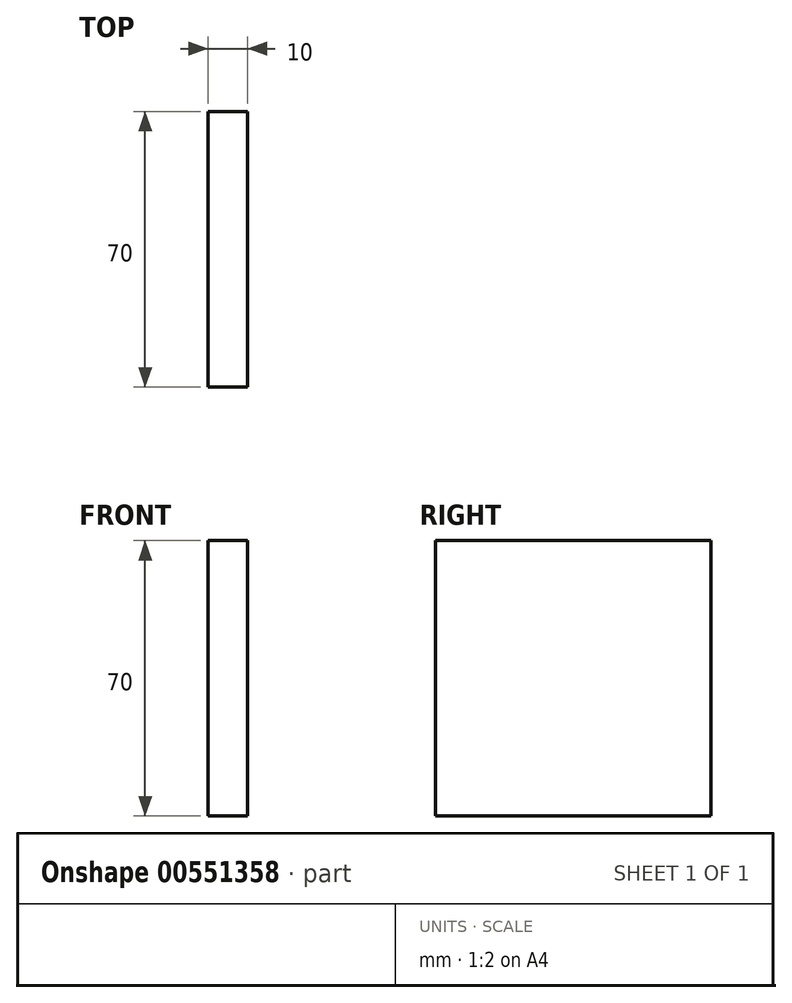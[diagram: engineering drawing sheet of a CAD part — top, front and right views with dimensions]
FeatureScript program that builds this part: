
annotation { "Feature Type Name" : "Feature", "Feature Type Description" : "" }
export const myFeature = defineFeature(function(context is Context, id is Id, definition is map)
    precondition{}
    {
        {
            var Q0;
            Q0=qCreatedBy(makeId("Right.planeOp"),FACE);
            var sketch = newSketch(context, id + "F0", { "sketchPlane" : qUnion([Q0])});
            skLineSegment(sketch, "E0.bottom", {"start": v(-149.8, 75.59) * mm, "end": v(-79.8, 75.59) * mm});
            skLineSegment(sketch, "E0.top", {"start": v(-149.8, 5.59) * mm, "end": v(-79.8, 5.59) * mm});
            skLineSegment(sketch, "E0.left", {"start": v(-149.8, 75.59) * mm, "end": v(-149.8, 5.59) * mm});
            skLineSegment(sketch, "E0.right", {"start": v(-79.8, 75.59) * mm, "end": v(-79.8, 5.59) * mm});
            skSolve(sketch);
        }
        {
            var Q0;
            Q0 = qSketchRegion(id + "F0", true);
            extrude(context, id + "F1", {"entities" : qUnion([Q0]), "depth" : 10 * mm, "offsetDistance" : 25 * mm});
        }
    });
